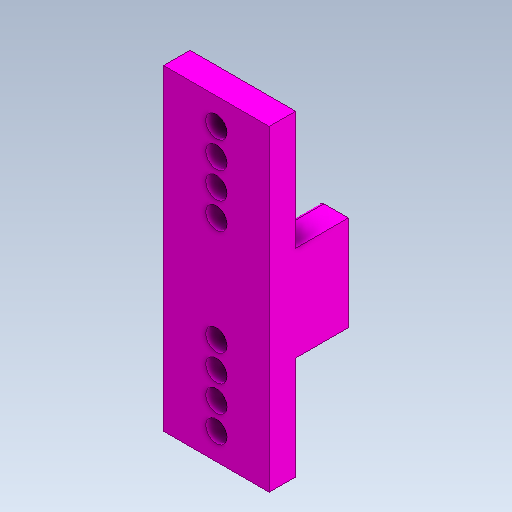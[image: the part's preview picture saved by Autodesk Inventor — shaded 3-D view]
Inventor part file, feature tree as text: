
AUTODESK INVENTOR PART (.ipt)
format: ipt  version: 2020 (Build 240168000, 168)  size: 128,512 bytes
history: native  units: in
note: dims shown in document units (in); Inventor stores cm internally (conversion verified against a paired STEP export)
features: other x3, sketch x3
ambient origin geometry x8: Origin, YZ Plane, XZ Plane, XY Plane, X Axis, Y Axis, Z Axis, Center Point
bodies: Solid1 (feature_tree)
feature tree (6):
  other  "ShaftRest.ipt"
  other  "Solid1::ShaftRest.ipt"
  other  "TaggingFeature1"
  sketch  "Sketch1"  dims[d0=0.3937in]
  sketch  "Sketch2"
  sketch  "Sketch3"
